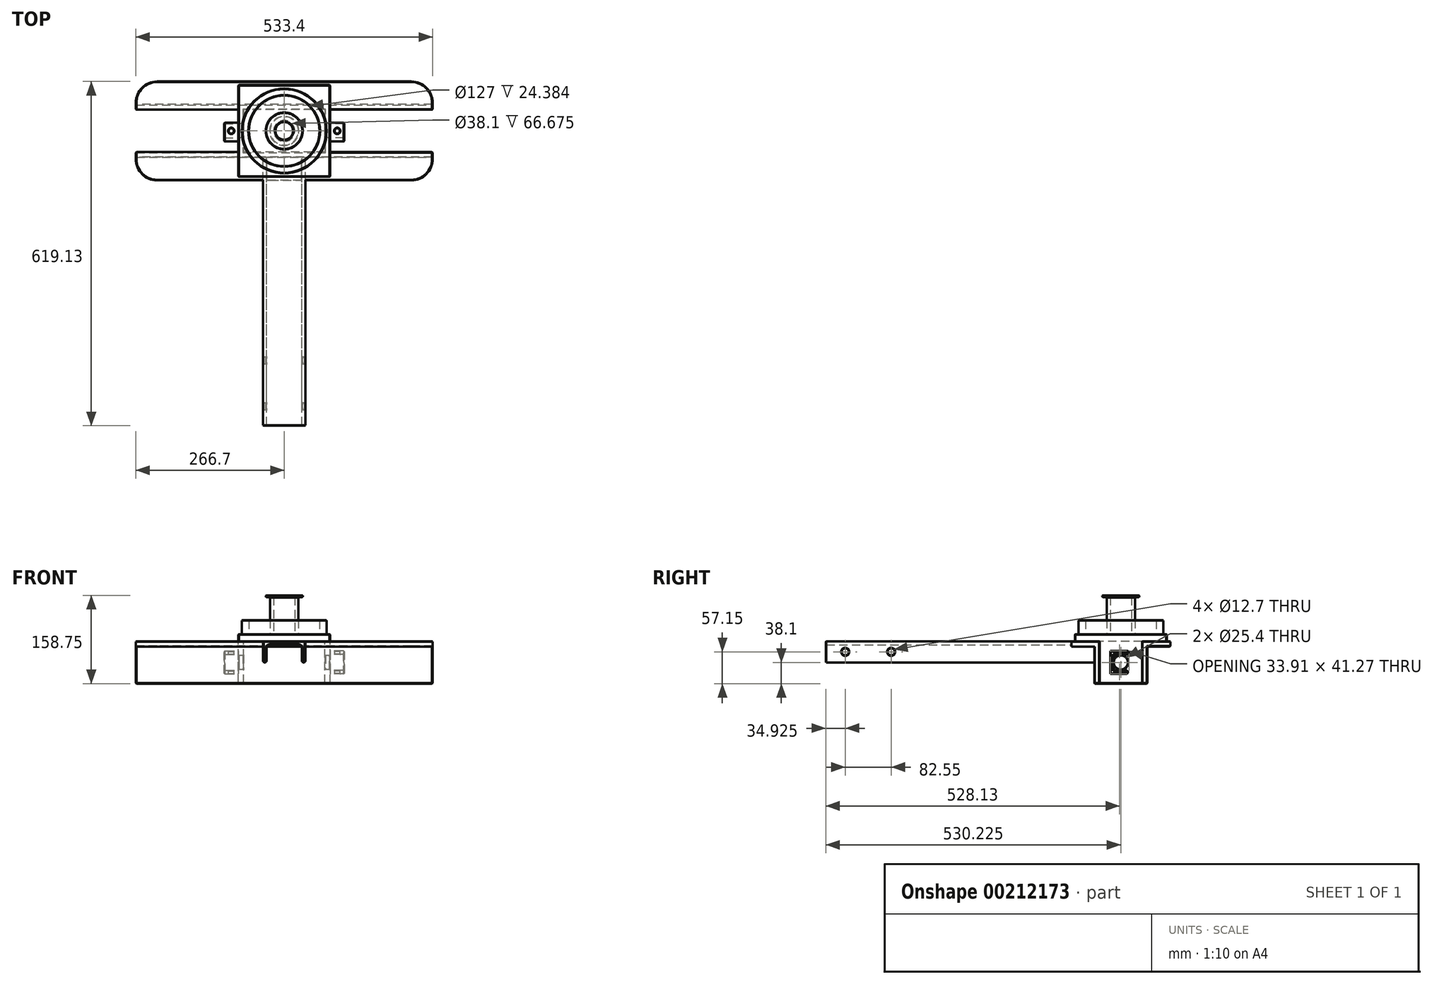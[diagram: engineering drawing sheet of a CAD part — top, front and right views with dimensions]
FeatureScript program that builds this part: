
annotation { "Feature Type Name" : "Feature", "Feature Type Description" : "" }
export const myFeature = defineFeature(function(context is Context, id is Id, definition is map)
    precondition{}
    {
        {
            var Q0;
            Q0=qCreatedBy(makeId("Front.planeOp"),FACE);
            var sketch = newSketch(context, id + "F0", { "sketchPlane" : qUnion([Q0])});
            skLineSegment(sketch, "E0", {"start": v(0, 0) * mm, "end": v(-38.1, 0) * mm, "construction": true});
            skLineSegment(sketch, "E1", {"start": v(-38.1, 0) * mm, "end": v(0, 0) * mm, "construction": true});
            skLineSegment(sketch, "E2", {"start": v(38.1, 0) * mm, "end": v(0, 0) * mm, "construction": true});
            skLineSegment(sketch, "E3", {"start": v(0, 38.1) * mm, "end": v(0, 0) * mm, "construction": true});
            skLineSegment(sketch, "E4", {"start": v(0, 38.1) * mm, "end": v(38.1, 38.1) * mm});
            skLineSegment(sketch, "E5", {"start": v(0, 38.1) * mm, "end": v(-38.1, 38.1) * mm});
            skLineSegment(sketch, "E6", {"start": v(-38.1, 38.1) * mm, "end": v(-38.1, 3.18) * mm});
            skLineSegment(sketch, "E7", {"start": v(38.1, 38.1) * mm, "end": v(38.1, 3.18) * mm});
            skLineSegment(sketch, "E8.0", {"start": v(0, 31.75) * mm, "end": v(25.4, 31.75) * mm});
            skLineSegment(sketch, "E9.0", {"start": v(0, 31.75) * mm, "end": v(-25.4, 31.75) * mm});
            skLineSegment(sketch, "E10.0", {"start": v(31.75, 25.4) * mm, "end": v(31.75, 3.18) * mm});
            skLineSegment(sketch, "E11.0", {"start": v(-31.75, 25.4) * mm, "end": v(-31.75, 3.18) * mm});
            skLineSegment(sketch, "E12", {"start": v(34.93, 0) * mm, "end": v(34.92, 0) * mm});
            skLineSegment(sketch, "E13", {"start": v(-34.93, 0) * mm, "end": v(-34.93, 0) * mm});
            skPoint(sketch, "E14.visualSharp", {"position": v(31.75, 31.75) * mm});
            skArc(sketch, "E14.filletArc", {"start": v(31.75, 25.4) * mm, "mid": v(29.9, 29.9) * mm, "end": v(25.4, 31.75) * mm});
            skPoint(sketch, "E15.visualSharp", {"position": v(-31.75, 31.75) * mm});
            skArc(sketch, "E15.filletArc", {"start": v(-25.4, 31.75) * mm, "mid": v(-29.9, 29.9) * mm, "end": v(-31.75, 25.4) * mm});
            skPoint(sketch, "E16.visualSharp", {"position": v(31.75, 0) * mm});
            skArc(sketch, "E16.filletArc", {"start": v(31.75, 3.18) * mm, "mid": v(32.68, 0.93) * mm, "end": v(34.92, 0) * mm});
            skPoint(sketch, "E17.visualSharp", {"position": v(38.1, 0) * mm});
            skArc(sketch, "E17.filletArc", {"start": v(34.93, 0) * mm, "mid": v(37.17, 0.93) * mm, "end": v(38.1, 3.18) * mm});
            skPoint(sketch, "E18.visualSharp", {"position": v(-31.75, 0) * mm});
            skArc(sketch, "E18.filletArc", {"start": v(-34.93, 0) * mm, "mid": v(-32.68, 0.93) * mm, "end": v(-31.75, 3.18) * mm});
            skPoint(sketch, "E19.visualSharp", {"position": v(-38.1, 0) * mm});
            skArc(sketch, "E19.filletArc", {"start": v(-38.1, 3.17) * mm, "mid": v(-37.17, 0.93) * mm, "end": v(-34.93, 0) * mm});
            skSolve(sketch);
        }
        {
            var Q0;
            Q0=makeQuery(id+"F0.imprint","IMPRINT",FACE,{"disambiguationData":[TD([[makeQuery(id+"F0.imprint","IMPRINT",EDGE,{"derivedFrom":sQuery(id+"F0.wireOp",EDGE,"E4")}),-1.0]])]});
            extrude(context, id + "F1", {"entities" : qUnion([Q0]), "depth" : 482.6 * mm});
        }
        {
            var Q0;
            Q0=makeQuery(id+"F1.opExtrude","SWEPT_FACE",FACE,{"disambiguationData":[OSD([sQuery(id+"F0.wireOp",EDGE,"E7")])]});
            var sketch = newSketch(context, id + "F2", { "sketchPlane" : qUnion([Q0])});
            skLineSegment(sketch, "E20.0", {"start": v(-482.6, 19.05) * mm, "end": v(0, 19.05) * mm, "construction": true});
            skCircle(sketch, "E21", {"center": v(-447.68, 19.05) * mm, "radius": 6.35 * mm});
            skCircle(sketch, "E22", {"center": v(-365.13, 19.05) * mm, "radius": 6.35 * mm});
            skLineSegment(sketch, "E23", {"start": v(0, 38.1) * mm, "end": v(0, 28.58) * mm, "construction": true});
            skLineSegment(sketch, "E24", {"start": v(0, 28.58) * mm, "end": v(8.16, 28.58) * mm, "construction": true});
            skLineSegment(sketch, "E25", {"start": v(0, 28.58) * mm, "end": v(-41.28, 28.58) * mm});
            skLineSegment(sketch, "E26", {"start": v(-41.28, 28.57) * mm, "end": v(-41.28, 38.1) * mm});
            skSolve(sketch);
        }
        {
            var Q0;
            {var subQ0=sQuery(id+"F2.wireOp",EDGE,"E25");Q0=makeQuery(id+"F2.imprint","IMPRINT",FACE,{"disambiguationData":[TD([[makeQuery(id+"F2.imprint","IMPRINT",EDGE,{"derivedFrom":subQ0}),-1.0]])]});}
            var Q1;
            Q1=makeQuery(id+"F2.imprint","IMPRINT",FACE,{"disambiguationData":[TD([[makeQuery(id+"F2.imprint","IMPRINT",EDGE,{"derivedFrom":sQuery(id+"F2.wireOp",EDGE,"E22")}),1.0]])]});
            var Q2;
            Q2=makeQuery(id+"F2.imprint","IMPRINT",FACE,{"disambiguationData":[TD([[makeQuery(id+"F2.imprint","IMPRINT",EDGE,{"derivedFrom":sQuery(id+"F2.wireOp",EDGE,"E21")}),1.0]])]});
            extrude(context, id + "F3", {"entities" : qUnion([Q0, Q1, Q2]), "operationType" : NewBodyOperationType.REMOVE, "endBound" : BoundingType.THROUGH_ALL, "oppositeDirection" : true, "depth" : 25.4 * mm});
        }
        {
            var Q0;
            Q0=makeQuery(id+"F1.opExtrude","SWEPT_FACE",FACE,{"disambiguationData":[OSD([sQuery(id+"F0.wireOp",EDGE,"E7")])]});
            var sketch = newSketch(context, id + "F4", { "sketchPlane" : qUnion([Q0])});
            skLineSegment(sketch, "E27", {"start": v(-41.28, 28.58) * mm, "end": v(-41.28, 38.1) * mm});
            skLineSegment(sketch, "E28", {"start": v(-41.28, 38.1) * mm, "end": v(9.52, 38.1) * mm});
            skLineSegment(sketch, "E29", {"start": v(9.52, 38.1) * mm, "end": v(9.53, -38.1) * mm});
            skLineSegment(sketch, "E30", {"start": v(9.53, -38.1) * mm, "end": v(0, -38.1) * mm});
            skLineSegment(sketch, "E31", {"start": v(0, -38.1) * mm, "end": v(0, 0) * mm});
            skLineSegment(sketch, "E32", {"start": v(-41.28, 28.58) * mm, "end": v(0, 28.58) * mm});
            skLineSegment(sketch, "E33", {"start": v(0, 28.58) * mm, "end": v(0, 0) * mm});
            skLineSegment(sketch, "E34", {"start": v(9.52, 38.1) * mm, "end": v(85.72, 38.1) * mm, "construction": true});
            skLineSegment(sketch, "E35", {"start": v(85.72, 38.1) * mm, "end": v(85.72, -38.1) * mm});
            skLineSegment(sketch, "E36", {"start": v(85.72, -38.1) * mm, "end": v(95.25, -38.1) * mm});
            skLineSegment(sketch, "E37", {"start": v(95.25, -38.1) * mm, "end": v(95.25, 28.58) * mm});
            skLineSegment(sketch, "E38", {"start": v(95.25, 28.58) * mm, "end": v(136.53, 28.58) * mm});
            skLineSegment(sketch, "E39", {"start": v(136.53, 28.58) * mm, "end": v(136.53, 38.1) * mm});
            skLineSegment(sketch, "E40", {"start": v(136.53, 38.1) * mm, "end": v(85.72, 38.1) * mm});
            skSolve(sketch);
        }
        {
            var Q0;
            Q0=makeQuery(id+"F4.imprint","IMPRINT",FACE,{"disambiguationData":[TD([[makeQuery(id+"F4.imprint","IMPRINT",EDGE,{"derivedFrom":sQuery(id+"F4.wireOp",EDGE,"E27")}),-1.0]])]});
            extrude(context, id + "F5", {"entities" : qUnion([Q0]), "operationType" : NewBodyOperationType.ADD, "depth" : 228.6 * mm, "hasSecondDirection" : true, "secondDirectionOppositeDirection" : true, "secondDirectionDepth" : 304.8 * mm});
        }
        {
            var Q0;
            Q0=makeQuery(id+"F5.boolean.opBoolean","MERGE",FACE,{"derivedFrom":[makeQuery(id+"F1.opExtrude","SWEPT_FACE",FACE,{"disambiguationData":[OSD([sQuery(id+"F0.wireOp",EDGE,"E4"),sQuery(id+"F0.wireOp",EDGE,"E5")])]}),makeQuery(id+"F5.opExtrude","SWEPT_FACE",FACE,{"disambiguationData":[OSD([sQuery(id+"F4.wireOp",EDGE,"E28")])]})]});
            var sketch = newSketch(context, id + "F6", { "sketchPlane" : qUnion([Q0])});
            skLineSegment(sketch, "E41", {"start": v(-38.1, -41.28) * mm, "end": v(38.1, -41.28) * mm, "construction": true});
            skPoint(sketch, "E42.endSnap0", {"position": v(0, -41.28) * mm});
            skLineSegment(sketch, "E43", {"start": v(0, -41.28) * mm, "end": v(0, 136.53) * mm, "construction": true});
            skLineSegment(sketch, "E44.bottom", {"start": v(82.55, 130.18) * mm, "end": v(-82.55, 130.18) * mm});
            skLineSegment(sketch, "E44.top", {"start": v(82.55, -34.92) * mm, "end": v(-82.55, -34.93) * mm});
            skLineSegment(sketch, "E44.left", {"start": v(82.55, 130.18) * mm, "end": v(82.55, -34.92) * mm});
            skLineSegment(sketch, "E44.right", {"start": v(-82.55, 130.18) * mm, "end": v(-82.55, -34.93) * mm});
            skPoint(sketch, "E44.middle", {"position": v(0, 47.62) * mm});
            skSolve(sketch);
        }
        {
            var Q0;
            {var subQ0=sQuery(id+"F6.wireOp",EDGE,"E44.bottom");Q0=makeQuery(id+"F6.imprint","IMPRINT",FACE,{"disambiguationData":[TD([[makeQuery(id+"F6.imprint","IMPRINT",EDGE,{"derivedFrom":subQ0}),1.0]])]});}
            var Q1;
            {var subQ0=sQuery(id+"F6.wireOp",EDGE,"E44.top");Q1=makeQuery(id+"F6.imprint","IMPRINT",FACE,{"disambiguationData":[TD([[makeQuery(id+"F6.imprint","IMPRINT",EDGE,{"derivedFrom":subQ0}),-1.0]])]});}
            extrude(context, id + "F7", {"entities" : qUnion([Q0, Q1]), "operationType" : NewBodyOperationType.ADD, "depth" : 12.7 * mm});
        }
        {
            var Q0;
            Q0=makeQuery(id+"F7.opExtrude","CAP_FACE",FACE,{"disambiguationData":[OSD([sQuery(id+"F6.wireOp",EDGE,"E44.bottom"),sQuery(id+"F6.wireOp",EDGE,"E44.top"),sQuery(id+"F6.wireOp",EDGE,"E44.left"),sQuery(id+"F6.wireOp",EDGE,"E44.right")])],"isStart":false});
            var sketch = newSketch(context, id + "F8", { "sketchPlane" : qUnion([Q0])});
            skLineSegment(sketch, "E45", {"start": v(-82.55, -34.93) * mm, "end": v(82.55, 130.18) * mm, "construction": true});
            skLineSegment(sketch, "E46", {"start": v(82.55, -34.92) * mm, "end": v(-82.55, 130.17) * mm, "construction": true});
            skCircle(sketch, "E47", {"center": v(0, 47.63) * mm, "radius": 76.2 * mm});
            skCircle(sketch, "E48", {"center": v(0, 47.63) * mm, "radius": 63.5 * mm});
            skCircle(sketch, "E49", {"center": v(0, 47.63) * mm, "radius": 25.4 * mm});
            skCircle(sketch, "E50", {"center": v(0, 47.63) * mm, "radius": 19.05 * mm});
            skCircle(sketch, "E51", {"center": v(0, 47.63) * mm, "radius": 33.34 * mm});
            skCircle(sketch, "E52", {"center": v(0, 47.63) * mm, "radius": 15.88 * mm});
            skSolve(sketch);
        }
        {
            var Q0;
            Q0=makeQuery(id+"F8.imprint","IMPRINT",FACE,{"disambiguationData":[TD([[makeQuery(id+"F8.imprint","IMPRINT",EDGE,{"derivedFrom":sQuery(id+"F8.wireOp",EDGE,"E47")}),1.0]])]});
            extrude(context, id + "F9", {"entities" : qUnion([Q0]), "operationType" : NewBodyOperationType.ADD, "depth" : 25.4 * mm});
        }
        {
            var Q0;
            Q0=makeQuery(id+"F8.imprint","IMPRINT",FACE,{"disambiguationData":[TD([[makeQuery(id+"F8.imprint","IMPRINT",EDGE,{"derivedFrom":sQuery(id+"F8.wireOp",EDGE,"E49")}),1.0]])]});
            extrude(context, id + "F10", {"entities" : qUnion([Q0]), "operationType" : NewBodyOperationType.ADD, "depth" : 66.67 * mm});
        }
        {
            var Q0;
            Q0=makeQuery(id+"F8.imprint","IMPRINT",FACE,{"disambiguationData":[TD([[makeQuery(id+"F8.imprint","IMPRINT",EDGE,{"derivedFrom":sQuery(id+"F8.wireOp",EDGE,"E49")}),-1.0]])]});
            var Q1;
            Q1=makeQuery(id+"F8.imprint","IMPRINT",FACE,{"disambiguationData":[TD([[makeQuery(id+"F8.imprint","IMPRINT",EDGE,{"derivedFrom":sQuery(id+"F8.wireOp",EDGE,"E49")}),1.0]])]});
            var Q2;
            Q2=makeQuery(id+"F8.imprint","IMPRINT",FACE,{"disambiguationData":[TD([[makeQuery(id+"F8.imprint","IMPRINT",EDGE,{"derivedFrom":sQuery(id+"F8.wireOp",EDGE,"E50")}),1.0]])]});
            extrude(context, id + "F11", {"entities" : qUnion([Q0, Q1, Q2]), "operationType" : NewBodyOperationType.ADD, "depth" : 69.85 * mm, "hasSecondDirection" : true, "secondDirectionOppositeDirection" : false, "secondDirectionDepth" : 66.67 * mm});
        }
        {
            var Q0;
            Q0=makeQuery(id+"F4.imprint","IMPRINT",FACE,{"disambiguationData":[TD([[makeQuery(id+"F4.imprint","IMPRINT",EDGE,{"derivedFrom":sQuery(id+"F4.wireOp",EDGE,"E35")}),1.0]])]});
            extrude(context, id + "F12", {"entities" : qUnion([Q0]), "operationType" : NewBodyOperationType.ADD, "depth" : 228.6 * mm, "hasSecondDirection" : true, "secondDirectionOppositeDirection" : true, "secondDirectionDepth" : 304.8 * mm});
        }
        {
            var Q0;
            Q0=makeQuery(id+"F7.opExtrude","CAP_FACE",FACE,{"disambiguationData":[OSD([sQuery(id+"F6.wireOp",EDGE,"E44.bottom"),sQuery(id+"F6.wireOp",EDGE,"E44.top"),sQuery(id+"F6.wireOp",EDGE,"E44.left"),sQuery(id+"F6.wireOp",EDGE,"E44.right")])],"isStart":true});
            var sketch = newSketch(context, id + "F13", { "sketchPlane" : qUnion([Q0])});
            skLineSegment(sketch, "E53.0", {"start": v(73.02, -85.72) * mm, "end": v(73.02, -9.52) * mm});
            skLineSegment(sketch, "E54.0", {"start": v(-73.03, -85.72) * mm, "end": v(-73.03, -9.52) * mm});
            skSolve(sketch);
        }
        {
            var Q0;
            {var subQ0=sQuery(id+"F13.wireOp",EDGE,"E54.0");Q0=makeQuery(id+"F13.imprint","IMPRINT",FACE,{"disambiguationData":[TD([[makeQuery(id+"F13.imprint","IMPRINT",EDGE,{"derivedFrom":subQ0}),1.0]])]});}
            var Q1;
            {var subQ0=sQuery(id+"F13.wireOp",EDGE,"E53.0");Q1=makeQuery(id+"F13.imprint","IMPRINT",FACE,{"disambiguationData":[TD([[makeQuery(id+"F13.imprint","IMPRINT",EDGE,{"derivedFrom":subQ0}),-1.0]])]});}
            var Q2;
            Q2=makeQuery(id+"F5.opExtrude","SWEPT_FACE",FACE,{"disambiguationData":[OSD([sQuery(id+"F4.wireOp",EDGE,"E30")])]});
            extrude(context, id + "F14", {"entities" : qUnion([Q0, Q1]), "operationType" : NewBodyOperationType.ADD, "endBound" : BoundingType.UP_TO_SURFACE, "endBoundEntityFace" : qUnion([Q2]), "depth" : 25.4 * mm});
        }
        {
            var Q0;
            {var subQ0=sQuery(id+"F6.wireOp",EDGE,"E44.right");Q0=makeQuery(id+"F14.boolean.opBoolean","MERGE",FACE,{"derivedFrom":[makeQuery(id+"F7.opExtrude","SWEPT_FACE",FACE,{"disambiguationData":[OSD([subQ0])]}),makeQuery(id+"F14.opExtrude","SWEPT_FACE",FACE,{"disambiguationData":[OSD([subQ0])]})]});}
            var sketch = newSketch(context, id + "F15", { "sketchPlane" : qUnion([Q0])});
            skLineSegment(sketch, "E55", {"start": v(-9.53, -38.1) * mm, "end": v(-85.72, 38.1) * mm, "construction": true});
            skLineSegment(sketch, "E56", {"start": v(-9.53, 38.1) * mm, "end": v(-85.72, -38.1) * mm, "construction": true});
            skCircle(sketch, "E57", {"center": v(-47.62, 0) * mm, "radius": 12.7 * mm});
            skLineSegment(sketch, "E58", {"start": v(-47.62, 0) * mm, "end": v(-34.92, 0) * mm, "construction": true});
            skLineSegment(sketch, "E59", {"start": v(-47.62, 0) * mm, "end": v(-47.62, -12.7) * mm, "construction": true});
            skLineSegment(sketch, "E60", {"start": v(-34.92, 0) * mm, "end": v(-28.57, 0) * mm, "construction": true});
            skLineSegment(sketch, "E61", {"start": v(-28.57, 0) * mm, "end": v(-28.57, 20.64) * mm});
            skLineSegment(sketch, "E62", {"start": v(-28.57, 0) * mm, "end": v(-28.57, -20.64) * mm});
            skLineSegment(sketch, "E63", {"start": v(-28.57, -20.64) * mm, "end": v(-57.15, -20.64) * mm});
            skLineSegment(sketch, "E64", {"start": v(-28.57, 20.64) * mm, "end": v(-59.31, 20.64) * mm});
            skLineSegment(sketch, "E65.0", {"start": v(-34.92, -14.29) * mm, "end": v(-57.15, -14.29) * mm});
            skLineSegment(sketch, "E66.0", {"start": v(-34.92, 14.29) * mm, "end": v(-59.31, 14.29) * mm});
            skLineSegment(sketch, "E67.0", {"start": v(-34.92, 0) * mm, "end": v(-34.92, 14.29) * mm});
            skLineSegment(sketch, "E68.0", {"start": v(-34.92, 0) * mm, "end": v(-34.92, -14.29) * mm});
            skLineSegment(sketch, "E69", {"start": v(-62.49, 17.46) * mm, "end": v(-62.49, 17.46) * mm});
            skLineSegment(sketch, "E70", {"start": v(-60.32, -17.46) * mm, "end": v(-60.32, -17.46) * mm});
            skPoint(sketch, "E71.visualSharp", {"position": v(-62.49, 20.64) * mm});
            skArc(sketch, "E71.filletArc", {"start": v(-59.31, 20.64) * mm, "mid": v(-61.56, 19.7) * mm, "end": v(-62.49, 17.46) * mm});
            skPoint(sketch, "E72.visualSharp", {"position": v(-62.49, 14.29) * mm});
            skArc(sketch, "E72.filletArc", {"start": v(-62.49, 17.46) * mm, "mid": v(-61.56, 15.22) * mm, "end": v(-59.31, 14.29) * mm});
            skPoint(sketch, "E73.visualSharp", {"position": v(-60.32, -14.29) * mm});
            skArc(sketch, "E73.filletArc", {"start": v(-57.15, -14.29) * mm, "mid": v(-59.4, -15.22) * mm, "end": v(-60.32, -17.46) * mm});
            skPoint(sketch, "E74.visualSharp", {"position": v(-60.32, -20.64) * mm});
            skArc(sketch, "E74.filletArc", {"start": v(-60.32, -17.46) * mm, "mid": v(-59.4, -19.7) * mm, "end": v(-57.15, -20.64) * mm});
            skSolve(sketch);
        }
        {
            var Q0;
            Q0=makeQuery(id+"F15.imprint","IMPRINT",FACE,{"disambiguationData":[TD([[makeQuery(id+"F15.imprint","IMPRINT",EDGE,{"derivedFrom":sQuery(id+"F15.wireOp",EDGE,"E57")}),1.0]])]});
            extrude(context, id + "F16", {"entities" : qUnion([Q0]), "operationType" : NewBodyOperationType.REMOVE, "endBound" : BoundingType.THROUGH_ALL, "oppositeDirection" : true, "depth" : 25.4 * mm});
        }
        {
            var Q0;
            Q0=makeQuery(id+"F15.imprint","IMPRINT",FACE,{"disambiguationData":[TD([[makeQuery(id+"F15.imprint","IMPRINT",EDGE,{"derivedFrom":sQuery(id+"F15.wireOp",EDGE,"E61")}),1.0]])]});
            extrude(context, id + "F17", {"entities" : qUnion([Q0]), "operationType" : NewBodyOperationType.ADD, "depth" : 25.4 * mm});
        }
        {
            var Q0;
            Q0=makeQuery(id+"F15.imprint","IMPRINT",FACE,{"disambiguationData":[TD([[makeQuery(id+"F15.imprint","IMPRINT",EDGE,{"derivedFrom":sQuery(id+"F15.wireOp",EDGE,"E61")}),1.0]])]});
            extrude(context, id + "F18", {"entities" : qUnion([Q0]), "operationType" : NewBodyOperationType.ADD, "oppositeDirection" : true, "depth" : 190.5 * mm, "hasSecondDirection" : true, "secondDirectionOppositeDirection" : true, "secondDirectionDepth" : 165.1 * mm});
        }
        {
            var Q0;
            Q0=makeQuery(id+"F18.opExtrude","SWEPT_FACE",FACE,{"disambiguationData":[OSD([sQuery(id+"F15.wireOp",EDGE,"E64")])]});
            var sketch = newSketch(context, id + "F19", { "sketchPlane" : qUnion([Q0])});
            skLineSegment(sketch, "E75", {"start": v(95.25, 47.62) * mm, "end": v(82.55, 47.62) * mm, "construction": true});
            skLineSegment(sketch, "E76", {"start": v(-82.55, 47.62) * mm, "end": v(-95.25, 47.62) * mm, "construction": true});
            skCircle(sketch, "E77", {"center": v(-95.25, 47.62) * mm, "radius": 4.76 * mm});
            skCircle(sketch, "E78", {"center": v(95.25, 47.62) * mm, "radius": 4.76 * mm});
            skSolve(sketch);
        }
        {
            var Q0;
            Q0=makeQuery(id+"F19.imprint","IMPRINT",FACE,{"disambiguationData":[TD([[makeQuery(id+"F19.imprint","IMPRINT",EDGE,{"derivedFrom":sQuery(id+"F19.wireOp",EDGE,"E77")}),1.0]])]});
            var Q1;
            Q1=makeQuery(id+"F19.imprint","IMPRINT",FACE,{"disambiguationData":[TD([[makeQuery(id+"F19.imprint","IMPRINT",EDGE,{"derivedFrom":sQuery(id+"F19.wireOp",EDGE,"E78")}),1.0]])]});
            extrude(context, id + "F20", {"entities" : qUnion([Q0, Q1]), "operationType" : NewBodyOperationType.REMOVE, "endBound" : BoundingType.THROUGH_ALL, "oppositeDirection" : true, "depth" : 25.4 * mm});
        }
        {
            var Q0;
            Q0=makeQuery(id+"F12.opExtrude","CAP_EDGE",EDGE,{"disambiguationData":[OSD([sQuery(id+"F4.wireOp",EDGE,"E39")])],"isStart":false});
            var Q1;
            Q1=makeQuery(id+"F5.opExtrude","CAP_EDGE",EDGE,{"disambiguationData":[OSD([sQuery(id+"F4.wireOp",EDGE,"E27")])],"isStart":false});
            var Q2;
            Q2=makeQuery(id+"F12.opExtrude","CAP_EDGE",EDGE,{"disambiguationData":[OSD([sQuery(id+"F4.wireOp",EDGE,"E39")])],"isStart":true});
            var Q3;
            Q3=makeQuery(id+"F5.opExtrude","CAP_EDGE",EDGE,{"disambiguationData":[OSD([sQuery(id+"F4.wireOp",EDGE,"E27")])],"isStart":true});
            fillet(context, id + "F21", {"entities" : qUnion([Q0, Q1, Q2, Q3]), "radius" : 38.1 * mm, "tangentPropagation" : true, "allowEdgeOverflow" : false});
        }
        {
            var Q0;
            Q0=makeQuery(id+"F9.opExtrude","CAP_FACE",FACE,{"disambiguationData":[OSD([sQuery(id+"F8.wireOp",EDGE,"E47"),sQuery(id+"F8.wireOp",EDGE,"E48")])],"isStart":false});
            var Q1;
            Q1=makeQuery(id+"F11.opExtrude","CAP_FACE",FACE,{"disambiguationData":[OSD([sQuery(id+"F8.wireOp",EDGE,"E51"),sQuery(id+"F8.wireOp",EDGE,"E52")])],"isStart":false});
            var Q2;
            {var subQ0=sQuery(id+"F8.wireOp",EDGE,"E51");Q2=makeQuery(id+"F11.boolean.opBoolean","SPLIT",FACE,{"disambiguationData":[TD([makeQuery(id+"F10.opExtrude","SWEPT_FACE",FACE,{"disambiguationData":[OSD([sQuery(id+"F8.wireOp",EDGE,"E49")])]})])],"derivedFrom":makeQuery(id+"F11.opExtrude","CAP_FACE",FACE,{"disambiguationData":[OSD([subQ0,sQuery(id+"F8.wireOp",EDGE,"E52")])],"isStart":true})});}
            var Q3;
            Q3=makeQuery(id+"F7.opExtrude","CAP_EDGE",EDGE,{"disambiguationData":[OSD([sQuery(id+"F6.wireOp",EDGE,"E44.right")])],"isStart":false});
            var Q4;
            Q4=makeQuery(id+"F7.opExtrude","CAP_EDGE",EDGE,{"disambiguationData":[OSD([sQuery(id+"F6.wireOp",EDGE,"E44.top")])],"isStart":false});
            var Q5;
            Q5=makeQuery(id+"F7.opExtrude","CAP_EDGE",EDGE,{"disambiguationData":[OSD([sQuery(id+"F6.wireOp",EDGE,"E44.bottom")])],"isStart":false});
            var Q6;
            Q6=makeQuery(id+"F7.opExtrude","CAP_EDGE",EDGE,{"disambiguationData":[OSD([sQuery(id+"F6.wireOp",EDGE,"E44.left")])],"isStart":false});
            var Q7;
            Q7=makeQuery(id+"F7.opExtrude","SWEPT_EDGE",EDGE,{"disambiguationData":[OSD([sQuery(id+"F6.wireOp",EDGE,"E44.top"),sQuery(id+"F6.wireOp",EDGE,"E44.right")])]});
            var Q8;
            Q8=makeQuery(id+"F7.opExtrude","SWEPT_EDGE",EDGE,{"disambiguationData":[OSD([sQuery(id+"F6.wireOp",EDGE,"E44.bottom"),sQuery(id+"F6.wireOp",EDGE,"E44.right")])]});
            var Q9;
            Q9=makeQuery(id+"F7.opExtrude","SWEPT_EDGE",EDGE,{"disambiguationData":[OSD([sQuery(id+"F6.wireOp",EDGE,"E44.top"),sQuery(id+"F6.wireOp",EDGE,"E44.left")])]});
            var Q10;
            Q10=makeQuery(id+"F7.opExtrude","SWEPT_EDGE",EDGE,{"disambiguationData":[OSD([sQuery(id+"F6.wireOp",EDGE,"E44.bottom"),sQuery(id+"F6.wireOp",EDGE,"E44.left")])]});
            var Q11;
            Q11=makeQuery(id+"F21.opFillet","BLEND_EDGE",EDGE,{"blendedFrom":[makeQuery(id+"F12.opExtrude","CAP_EDGE",EDGE,{"disambiguationData":[OSD([sQuery(id+"F4.wireOp",EDGE,"E39")])],"isStart":false}),makeQuery(id+"F12.opExtrude","SWEPT_FACE",FACE,{"disambiguationData":[OSD([sQuery(id+"F4.wireOp",EDGE,"E40")])]})],"blendedInto":[makeQuery(id+"F12.opExtrude","SWEPT_FACE",FACE,{"disambiguationData":[OSD([sQuery(id+"F4.wireOp",EDGE,"E40")])]})]});
            var Q12;
            Q12=makeQuery(id+"F12.opExtrude","CAP_EDGE",EDGE,{"disambiguationData":[OSD([sQuery(id+"F4.wireOp",EDGE,"E40")])],"isStart":false});
            var Q13;
            Q13=makeQuery(id+"F12.opExtrude","SWEPT_EDGE",EDGE,{"disambiguationData":[OSD([sQuery(id+"F4.wireOp",EDGE,"E39"),sQuery(id+"F4.wireOp",EDGE,"E40")])]});
            var Q14;
            {var subQ0=sQuery(id+"F4.wireOp",EDGE,"E40");var subQ1=sQuery(id+"F4.wireOp",EDGE,"E35");var subQ2=sQuery(id+"F6.wireOp",EDGE,"E44.left");Q14=makeQuery(id+"F12.boolean.opBoolean","SPLIT",EDGE,{"disambiguationData":[TD([makeQuery(id+"F7.opExtrude","CAP_FACE",FACE,{"disambiguationData":[OSD([sQuery(id+"F6.wireOp",EDGE,"E44.bottom"),sQuery(id+"F6.wireOp",EDGE,"E44.top"),subQ2,sQuery(id+"F6.wireOp",EDGE,"E44.right")])],"isStart":true}),makeQuery(id+"F7.opExtrude","SWEPT_FACE",FACE,{"disambiguationData":[OSD([subQ2])]}),makeQuery(id+"F12.opExtrude","SWEPT_FACE",FACE,{"disambiguationData":[OSD([subQ1])]}),makeQuery(id+"F12.opExtrude","CAP_FACE",FACE,{"disambiguationData":[OSD([subQ1,sQuery(id+"F4.wireOp",EDGE,"E36"),sQuery(id+"F4.wireOp",EDGE,"E37"),sQuery(id+"F4.wireOp",EDGE,"E38"),sQuery(id+"F4.wireOp",EDGE,"E39"),subQ0])],"isStart":false}),makeQuery(id+"F12.opExtrude","SWEPT_FACE",FACE,{"disambiguationData":[OSD([subQ0])]})])],"derivedFrom":makeQuery(id+"F12.opExtrude","SWEPT_EDGE",EDGE,{"disambiguationData":[OSD([subQ1,subQ0])]})});}
            var Q15;
            Q15=makeQuery(id+"F21.opFillet","BLEND_EDGE",EDGE,{"blendedFrom":[makeQuery(id+"F12.opExtrude","CAP_EDGE",EDGE,{"disambiguationData":[OSD([sQuery(id+"F4.wireOp",EDGE,"E39")])],"isStart":true}),makeQuery(id+"F12.opExtrude","SWEPT_FACE",FACE,{"disambiguationData":[OSD([sQuery(id+"F4.wireOp",EDGE,"E40")])]})],"blendedInto":[makeQuery(id+"F12.opExtrude","SWEPT_FACE",FACE,{"disambiguationData":[OSD([sQuery(id+"F4.wireOp",EDGE,"E40")])]})]});
            var Q16;
            Q16=makeQuery(id+"F12.opExtrude","CAP_EDGE",EDGE,{"disambiguationData":[OSD([sQuery(id+"F4.wireOp",EDGE,"E40")])],"isStart":true});
            var Q17;
            Q17=makeQuery(id+"F5.opExtrude","CAP_EDGE",EDGE,{"disambiguationData":[OSD([sQuery(id+"F4.wireOp",EDGE,"E28")])],"isStart":true});
            var Q18;
            Q18=makeQuery(id+"F12.opExtrude","CAP_EDGE",EDGE,{"disambiguationData":[OSD([sQuery(id+"F4.wireOp",EDGE,"E35")])],"isStart":true});
            var Q19;
            Q19=makeQuery(id+"F12.opExtrude","CAP_EDGE",EDGE,{"disambiguationData":[OSD([sQuery(id+"F4.wireOp",EDGE,"E37")])],"isStart":true});
            var Q20;
            Q20=makeQuery(id+"F12.opExtrude","CAP_EDGE",EDGE,{"disambiguationData":[OSD([sQuery(id+"F4.wireOp",EDGE,"E36")])],"isStart":true});
            var Q21;
            Q21=makeQuery(id+"F5.opExtrude","CAP_EDGE",EDGE,{"disambiguationData":[OSD([sQuery(id+"F4.wireOp",EDGE,"E29")])],"isStart":true});
            var Q22;
            Q22=makeQuery(id+"F5.opExtrude","CAP_EDGE",EDGE,{"disambiguationData":[OSD([sQuery(id+"F4.wireOp",EDGE,"E30")])],"isStart":true});
            var Q23;
            Q23=makeQuery(id+"F5.opExtrude","CAP_EDGE",EDGE,{"disambiguationData":[OSD([sQuery(id+"F4.wireOp",EDGE,"E31"),sQuery(id+"F4.wireOp",EDGE,"E33")])],"isStart":true});
            var Q24;
            Q24=makeQuery(id+"F5.opExtrude","CAP_EDGE",EDGE,{"disambiguationData":[OSD([sQuery(id+"F4.wireOp",EDGE,"E28")])],"isStart":false});
            var Q25;
            {var subQ0=sQuery(id+"F4.wireOp",EDGE,"E29");var subQ1=sQuery(id+"F4.wireOp",EDGE,"E28");var subQ2=sQuery(id+"F6.wireOp",EDGE,"E44.left");Q25=makeQuery(id+"F7.boolean.opBoolean","SPLIT",EDGE,{"disambiguationData":[TD([makeQuery(id+"F1.opExtrude","SWEPT_FACE",FACE,{"disambiguationData":[OSD([sQuery(id+"F0.wireOp",EDGE,"E4"),sQuery(id+"F0.wireOp",EDGE,"E5")])]}),makeQuery(id+"F5.opExtrude","CAP_FACE",FACE,{"disambiguationData":[OSD([sQuery(id+"F4.wireOp",EDGE,"E27"),subQ1,subQ0,sQuery(id+"F4.wireOp",EDGE,"E30"),sQuery(id+"F4.wireOp",EDGE,"E31"),sQuery(id+"F4.wireOp",EDGE,"E32"),sQuery(id+"F4.wireOp",EDGE,"E33")])],"isStart":false}),makeQuery(id+"F5.opExtrude","SWEPT_FACE",FACE,{"disambiguationData":[OSD([subQ1])]}),makeQuery(id+"F5.opExtrude","SWEPT_FACE",FACE,{"disambiguationData":[OSD([subQ0])]}),makeQuery(id+"F7.opExtrude","CAP_FACE",FACE,{"disambiguationData":[OSD([sQuery(id+"F6.wireOp",EDGE,"E44.bottom"),sQuery(id+"F6.wireOp",EDGE,"E44.top"),subQ2,sQuery(id+"F6.wireOp",EDGE,"E44.right")])],"isStart":true}),makeQuery(id+"F7.opExtrude","SWEPT_FACE",FACE,{"disambiguationData":[OSD([subQ2])]})])],"derivedFrom":makeQuery(id+"F5.opExtrude","SWEPT_EDGE",EDGE,{"disambiguationData":[OSD([subQ1,subQ0])]})});}
            var Q26;
            Q26=makeQuery(id+"F5.opExtrude","CAP_EDGE",EDGE,{"disambiguationData":[OSD([sQuery(id+"F4.wireOp",EDGE,"E29")])],"isStart":false});
            var Q27;
            Q27=makeQuery(id+"F5.opExtrude","CAP_EDGE",EDGE,{"disambiguationData":[OSD([sQuery(id+"F4.wireOp",EDGE,"E31"),sQuery(id+"F4.wireOp",EDGE,"E33")])],"isStart":false});
            var Q28;
            Q28=makeQuery(id+"F5.opExtrude","CAP_EDGE",EDGE,{"disambiguationData":[OSD([sQuery(id+"F4.wireOp",EDGE,"E30")])],"isStart":false});
            var Q29;
            Q29=makeQuery(id+"F12.opExtrude","CAP_EDGE",EDGE,{"disambiguationData":[OSD([sQuery(id+"F4.wireOp",EDGE,"E35")])],"isStart":false});
            var Q30;
            Q30=makeQuery(id+"F12.opExtrude","CAP_EDGE",EDGE,{"disambiguationData":[OSD([sQuery(id+"F4.wireOp",EDGE,"E36")])],"isStart":false});
            var Q31;
            Q31=makeQuery(id+"F12.opExtrude","CAP_EDGE",EDGE,{"disambiguationData":[OSD([sQuery(id+"F4.wireOp",EDGE,"E37")])],"isStart":false});
            var Q32;
            Q32=makeQuery(id+"F21.opFillet","BLEND_EDGE",EDGE,{"blendedFrom":[makeQuery(id+"F12.opExtrude","CAP_EDGE",EDGE,{"disambiguationData":[OSD([sQuery(id+"F4.wireOp",EDGE,"E39")])],"isStart":false}),makeQuery(id+"F12.opExtrude","SWEPT_FACE",FACE,{"disambiguationData":[OSD([sQuery(id+"F4.wireOp",EDGE,"E38")])]})],"blendedInto":[makeQuery(id+"F12.opExtrude","SWEPT_FACE",FACE,{"disambiguationData":[OSD([sQuery(id+"F4.wireOp",EDGE,"E38")])]})]});
            var Q33;
            {var subQ0=sQuery(id+"F4.wireOp",EDGE,"E40");var subQ1=sQuery(id+"F4.wireOp",EDGE,"E35");var subQ2=sQuery(id+"F4.wireOp",EDGE,"E29");var subQ3=sQuery(id+"F4.wireOp",EDGE,"E28");var subQ4=sQuery(id+"F4.wireOp",EDGE,"E30");Q33=makeQuery(id+"F14.boolean.opBoolean","MERGE",FACE,{"derivedFrom":[makeQuery(id+"F5.opExtrude","SWEPT_FACE",FACE,{"disambiguationData":[OSD([subQ4])]}),makeQuery(id+"F12.opExtrude","SWEPT_FACE",FACE,{"disambiguationData":[OSD([sQuery(id+"F4.wireOp",EDGE,"E36")])]}),makeQuery(id+"F14.opExtrude","CAP_FACE",FACE,{"disambiguationData":[OSD([subQ4]),ownerDisambiguation([makeQuery(id+"F14.opExtrude","SWEPT_BODY",BODY,{"disambiguationData":[OSD([subQ3,subQ2,subQ1,subQ0,sQuery(id+"F6.wireOp",EDGE,"E44.left"),sQuery(id+"F13.wireOp",EDGE,"E53.0")])]})])],"isStart":false}),makeQuery(id+"F14.opExtrude","CAP_FACE",FACE,{"disambiguationData":[OSD([subQ4]),ownerDisambiguation([makeQuery(id+"F14.opExtrude","SWEPT_BODY",BODY,{"disambiguationData":[OSD([subQ3,subQ2,subQ1,subQ0,sQuery(id+"F6.wireOp",EDGE,"E44.right"),sQuery(id+"F13.wireOp",EDGE,"E54.0")])]})])],"isStart":false})]});}
            var Q34;
            Q34=makeQuery(id+"F17.opExtrude","CAP_FACE",FACE,{"disambiguationData":[OSD([sQuery(id+"F15.wireOp",EDGE,"E61"),sQuery(id+"F15.wireOp",EDGE,"E62"),sQuery(id+"F15.wireOp",EDGE,"E63"),sQuery(id+"F15.wireOp",EDGE,"E64"),sQuery(id+"F15.wireOp",EDGE,"E65.0"),sQuery(id+"F15.wireOp",EDGE,"E66.0"),sQuery(id+"F15.wireOp",EDGE,"E67.0"),sQuery(id+"F15.wireOp",EDGE,"E68.0"),sQuery(id+"F15.wireOp",EDGE,"E71.filletArc"),sQuery(id+"F15.wireOp",EDGE,"E72.filletArc"),sQuery(id+"F15.wireOp",EDGE,"E73.filletArc"),sQuery(id+"F15.wireOp",EDGE,"E74.filletArc")])],"isStart":false});
            var Q35;
            Q35=makeQuery(id+"F20.boolean.opBoolean","COPY",FACE,{"disambiguationData":[TD([makeQuery(id+"F17.opExtrude","SWEPT_FACE",FACE,{"disambiguationData":[OSD([sQuery(id+"F15.wireOp",EDGE,"E63")])]})])],"derivedFrom":makeQuery(id+"F20.opExtrude","SWEPT_FACE",FACE,{"disambiguationData":[OSD([sQuery(id+"F19.wireOp",EDGE,"E77")])]})});
            var Q36;
            Q36=makeQuery(id+"F20.boolean.opBoolean","COPY",FACE,{"disambiguationData":[TD([makeQuery(id+"F17.opExtrude","SWEPT_FACE",FACE,{"disambiguationData":[OSD([sQuery(id+"F15.wireOp",EDGE,"E64")])]})])],"derivedFrom":makeQuery(id+"F20.opExtrude","SWEPT_FACE",FACE,{"disambiguationData":[OSD([sQuery(id+"F19.wireOp",EDGE,"E77")])]})});
            var Q37;
            {var subQ0=sQuery(id+"F6.wireOp",EDGE,"E44.right");Q37=makeQuery(id+"F16.boolean.opBoolean","COPY",FACE,{"disambiguationData":[TD([makeQuery(id+"F7.opExtrude","SWEPT_FACE",FACE,{"disambiguationData":[OSD([subQ0])]})])],"derivedFrom":makeQuery(id+"F16.opExtrude","SWEPT_FACE",FACE,{"disambiguationData":[OSD([sQuery(id+"F15.wireOp",EDGE,"E57")])]})});}
            var Q38;
            {var subQ0=sQuery(id+"F6.wireOp",EDGE,"E44.left");Q38=makeQuery(id+"F16.boolean.opBoolean","COPY",FACE,{"disambiguationData":[TD([makeQuery(id+"F7.opExtrude","SWEPT_FACE",FACE,{"disambiguationData":[OSD([subQ0])]})])],"derivedFrom":makeQuery(id+"F16.opExtrude","SWEPT_FACE",FACE,{"disambiguationData":[OSD([sQuery(id+"F15.wireOp",EDGE,"E57")])]})});}
            var Q39;
            Q39=makeQuery(id+"F20.boolean.opBoolean","COPY",FACE,{"disambiguationData":[TD([makeQuery(id+"F18.opExtrude","SWEPT_FACE",FACE,{"disambiguationData":[OSD([sQuery(id+"F15.wireOp",EDGE,"E64")])]})])],"derivedFrom":makeQuery(id+"F20.opExtrude","SWEPT_FACE",FACE,{"disambiguationData":[OSD([sQuery(id+"F19.wireOp",EDGE,"E78")])]})});
            var Q40;
            Q40=makeQuery(id+"F20.boolean.opBoolean","COPY",FACE,{"disambiguationData":[TD([makeQuery(id+"F18.opExtrude","SWEPT_FACE",FACE,{"disambiguationData":[OSD([sQuery(id+"F15.wireOp",EDGE,"E63")])]})])],"derivedFrom":makeQuery(id+"F20.opExtrude","SWEPT_FACE",FACE,{"disambiguationData":[OSD([sQuery(id+"F19.wireOp",EDGE,"E78")])]})});
            var Q41;
            Q41=makeQuery(id+"F18.opExtrude","CAP_FACE",FACE,{"disambiguationData":[OSD([sQuery(id+"F15.wireOp",EDGE,"E61"),sQuery(id+"F15.wireOp",EDGE,"E62"),sQuery(id+"F15.wireOp",EDGE,"E63"),sQuery(id+"F15.wireOp",EDGE,"E64"),sQuery(id+"F15.wireOp",EDGE,"E65.0"),sQuery(id+"F15.wireOp",EDGE,"E66.0"),sQuery(id+"F15.wireOp",EDGE,"E67.0"),sQuery(id+"F15.wireOp",EDGE,"E68.0"),sQuery(id+"F15.wireOp",EDGE,"E71.filletArc"),sQuery(id+"F15.wireOp",EDGE,"E72.filletArc"),sQuery(id+"F15.wireOp",EDGE,"E73.filletArc"),sQuery(id+"F15.wireOp",EDGE,"E74.filletArc")])],"isStart":false});
            var Q42;
            Q42=makeQuery(id+"F1.opExtrude","CAP_FACE",FACE,{"disambiguationData":[OSD([sQuery(id+"F0.wireOp",EDGE,"E4"),sQuery(id+"F0.wireOp",EDGE,"E5"),sQuery(id+"F0.wireOp",EDGE,"E6"),sQuery(id+"F0.wireOp",EDGE,"E7"),sQuery(id+"F0.wireOp",EDGE,"E8.0"),sQuery(id+"F0.wireOp",EDGE,"E9.0"),sQuery(id+"F0.wireOp",EDGE,"E10.0"),sQuery(id+"F0.wireOp",EDGE,"E11.0"),sQuery(id+"F0.wireOp",EDGE,"E14.filletArc"),sQuery(id+"F0.wireOp",EDGE,"E15.filletArc"),sQuery(id+"F0.wireOp",EDGE,"E16.filletArc"),sQuery(id+"F0.wireOp",EDGE,"E17.filletArc"),sQuery(id+"F0.wireOp",EDGE,"E18.filletArc"),sQuery(id+"F0.wireOp",EDGE,"E19.filletArc")])],"isStart":false});
            var Q43;
            Q43=makeQuery(id+"F3.boolean.opBoolean","COPY",FACE,{"disambiguationData":[TD([makeQuery(id+"F1.opExtrude","SWEPT_FACE",FACE,{"disambiguationData":[OSD([sQuery(id+"F0.wireOp",EDGE,"E7")])]})])],"derivedFrom":makeQuery(id+"F3.opExtrude","SWEPT_FACE",FACE,{"disambiguationData":[OSD([sQuery(id+"F2.wireOp",EDGE,"E22")])]})});
            var Q44;
            Q44=makeQuery(id+"F3.boolean.opBoolean","COPY",FACE,{"disambiguationData":[TD([makeQuery(id+"F1.opExtrude","SWEPT_FACE",FACE,{"disambiguationData":[OSD([sQuery(id+"F0.wireOp",EDGE,"E7")])]})])],"derivedFrom":makeQuery(id+"F3.opExtrude","SWEPT_FACE",FACE,{"disambiguationData":[OSD([sQuery(id+"F2.wireOp",EDGE,"E21")])]})});
            var Q45;
            Q45=makeQuery(id+"F3.boolean.opBoolean","COPY",FACE,{"disambiguationData":[TD([makeQuery(id+"F1.opExtrude","SWEPT_FACE",FACE,{"disambiguationData":[OSD([sQuery(id+"F0.wireOp",EDGE,"E6")])]})])],"derivedFrom":makeQuery(id+"F3.opExtrude","SWEPT_FACE",FACE,{"disambiguationData":[OSD([sQuery(id+"F2.wireOp",EDGE,"E21")])]})});
            var Q46;
            Q46=makeQuery(id+"F3.boolean.opBoolean","COPY",FACE,{"disambiguationData":[TD([makeQuery(id+"F1.opExtrude","SWEPT_FACE",FACE,{"disambiguationData":[OSD([sQuery(id+"F0.wireOp",EDGE,"E6")])]})])],"derivedFrom":makeQuery(id+"F3.opExtrude","SWEPT_FACE",FACE,{"disambiguationData":[OSD([sQuery(id+"F2.wireOp",EDGE,"E22")])]})});
            chamfer(context, id + "F22", {"entities" : qUnion([Q0, Q1, Q2, Q3, Q4, Q5, Q6, Q7, Q8, Q9, Q10, Q11, Q12, Q13, Q14, Q15, Q16, Q17, Q18, Q19, Q20, Q21, Q22, Q23, Q24, Q25, Q26, Q27, Q28, Q29, Q30, Q31, Q32, Q33, Q34, Q35, Q36, Q37, Q38, Q39, Q40, Q41, Q42, Q43, Q44, Q45, Q46]), "width" : 1.02 * mm, "tangentPropagation" : true});
        }
    });
